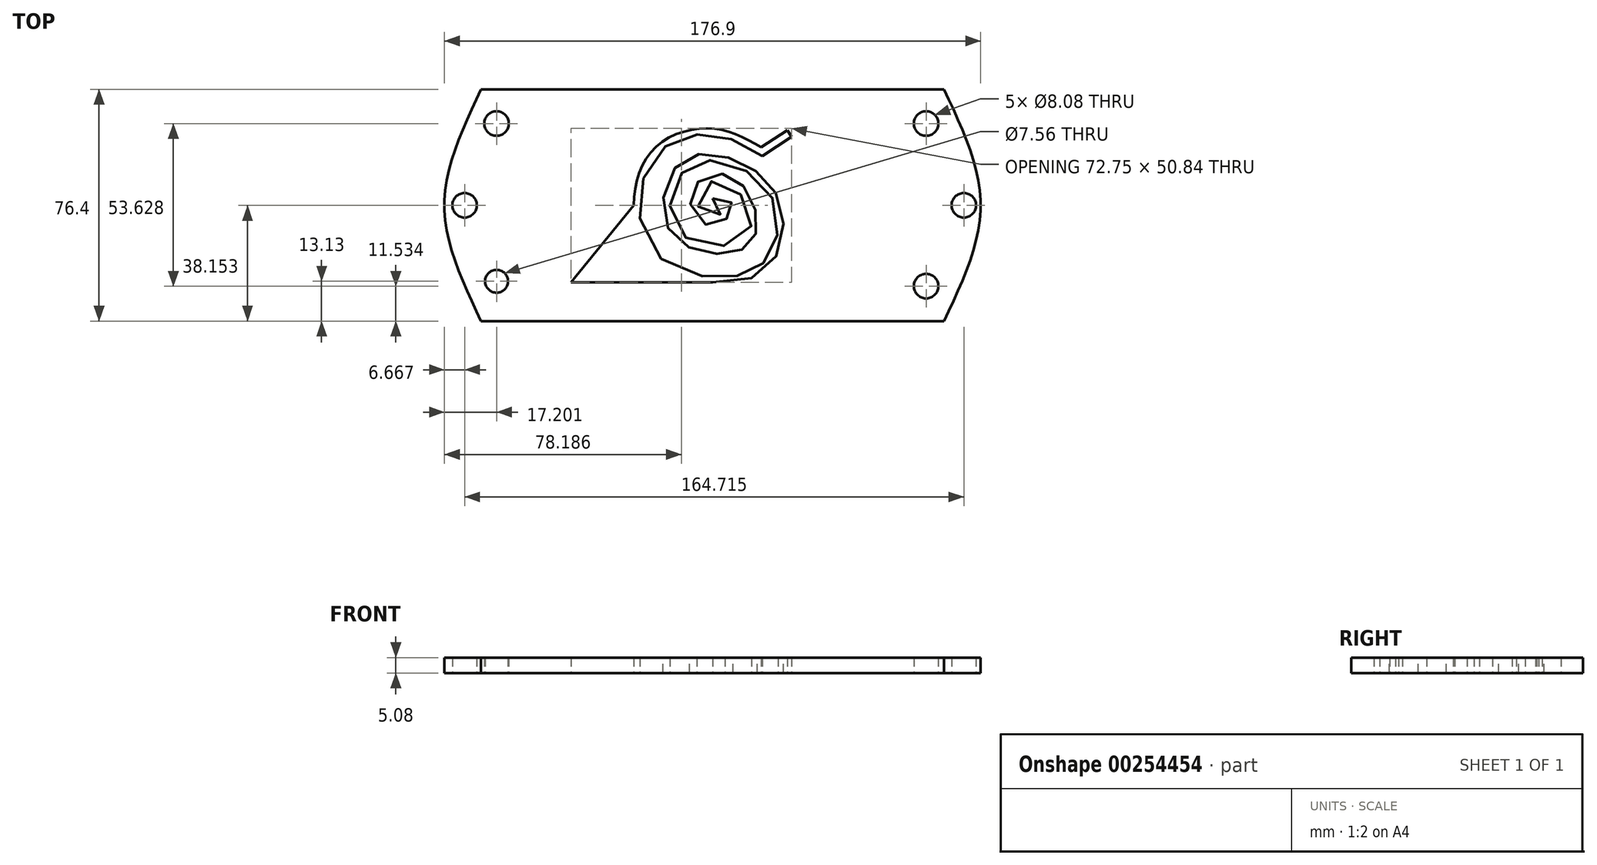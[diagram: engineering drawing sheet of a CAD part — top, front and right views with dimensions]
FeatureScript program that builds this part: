
annotation { "Feature Type Name" : "Feature", "Feature Type Description" : "" }
export const myFeature = defineFeature(function(context is Context, id is Id, definition is map)
    precondition{}
    {
        {
            var Q0;
            Q0=qCreatedBy(makeId("Top.planeOp"),FACE);
            var sketch = newSketch(context, id + "F0", { "sketchPlane" : qUnion([Q0])});
            skLineSegment(sketch, "E0.top", {"start": v(0, 38.2) * mm, "end": v(-76.4, 38.2) * mm});
            skLineSegment(sketch, "E1.MirrorCS", {"start": v(0, -38.2) * mm, "end": v(-76.4, -38.2) * mm});
            skFitSpline(sketch, "E2", {"points": [v(-76.4, 38.2) * mm, v(-88.45, 0) * mm, v(-76.4, -38.2) * mm], "startDerivative": vector(-36.19, -76.4) * mm, "endDerivative": vector(36.19, -76.4) * mm});
            skPoint(sketch, "E3.MirrorCS.start.orphan", {"position": v(-76.4, 0) * mm});
            skPoint(sketch, "E4.MirrorP", {"position": v(76.4, 0) * mm});
            skFitSpline(sketch, "E5.MirrorCS", {"points": [v(76.4, 38.2) * mm, v(88.45, 0) * mm, v(76.4, -38.2) * mm], "startDerivative": vector(36.19, -76.4) * mm, "endDerivative": vector(-36.19, -76.4) * mm});
            skLineSegment(sketch, "E6.MirrorCS", {"start": v(0, 38.2) * mm, "end": v(76.4, 38.2) * mm});
            skLineSegment(sketch, "E7.MirrorCS", {"start": v(0, -38.2) * mm, "end": v(76.4, -38.2) * mm});
            skPoint(sketch, "E8.MirrorCS.end.orphan", {"position": v(0, 38.2) * mm});
            skPoint(sketch, "E8.MirrorCS.start.orphan", {"position": v(0, 0) * mm});
            skLineSegment(sketch, "E9", {"start": v(16.08, 19.16) * mm, "end": v(24.66, 24.8) * mm});
            skFitSpline(sketch, "E10", {"points": [v(16.08, 19.16) * mm, v(0, 25.33) * mm, v(-18.76, 19.16) * mm, v(-26, 0) * mm, v(-17.15, -19.7) * mm, v(16.08, -22.38) * mm, v(22.52, 0) * mm, v(8.3, 14.6) * mm, v(-10.45, 14.34) * mm, v(-15.28, -6.3) * mm, v(0, -15.95) * mm, v(12.87, -12.2) * mm, v(13.67, 0) * mm, v(3.48, 10.32) * mm, v(-7.5, 3.35) * mm, v(0, -6.84) * mm, v(6.7, 0) * mm, v(0, 2.28) * mm], "startDerivative": vector(-255.12, 143) * mm, "endDerivative": vector(-251.77, 14.65) * mm});
            skLineSegment(sketch, "E11", {"start": v(0, -25.47) * mm, "end": v(-46.64, -25.47) * mm});
            skLineSegment(sketch, "E12", {"start": v(-26, 0) * mm, "end": v(-46.64, -25.47) * mm});
            skCircle(sketch, "E13", {"center": v(-71.25, 26.96) * mm, "radius": 4.04 * mm});
            skCircle(sketch, "E14", {"center": v(-81.78, 0) * mm, "radius": 4.04 * mm});
            skCircle(sketch, "E15", {"center": v(-71.25, -25.07) * mm, "radius": 3.78 * mm});
            skCircle(sketch, "E16", {"center": v(70.48, 26.96) * mm, "radius": 4.04 * mm});
            skCircle(sketch, "E17", {"center": v(82.93, 0) * mm, "radius": 4.04 * mm});
            skCircle(sketch, "E18", {"center": v(70.48, -26.67) * mm, "radius": 4.04 * mm});
            skFitSpline(sketch, "E19", {"points": [v(-18.35, 81.74) * mm, v(-34.43, 87.9) * mm, v(-53.2, 81.74) * mm, v(-60.43, 62.57) * mm, v(-51.59, 42.87) * mm, v(-18.35, 40.2) * mm, v(-11.92, 62.57) * mm, v(-26.12, 77.18) * mm, v(-44.89, 76.91) * mm, v(-49.71, 56.27) * mm, v(-34.43, 46.62) * mm, v(-21.57, 50.38) * mm, v(-20.76, 62.57) * mm, v(-30.95, 72.9) * mm, v(-41.94, 65.92) * mm, v(-34.43, 55.74) * mm, v(-27.73, 62.57) * mm, v(-34.43, 64.85) * mm], "startDerivative": vector(-255.12, 143) * mm, "endDerivative": vector(-251.77, 14.65) * mm});
            skLineSegment(sketch, "E20", {"start": v(24.66, 24.8) * mm, "end": v(26.11, 22.58) * mm});
            skLineSegment(sketch, "E21", {"start": v(26.11, 22.58) * mm, "end": v(17.92, 17.2) * mm});
            skLineSegment(sketch, "E22", {"start": v(17.92, 17.2) * mm, "end": v(16.38, 16.2) * mm});
            skFitSpline(sketch, "E23", {"points": [v(16.38, 16.2) * mm, v(9.76, 20.15) * mm, v(2.94, 22.91) * mm, v(-4.42, 23.46) * mm, v(-11.8, 21.62) * mm, v(-17.5, 17.75) * mm, v(-22.66, 9.28) * mm, v(-23.95, 0) * mm, v(-22.3, -10.98) * mm, v(-11.6, -21.1) * mm, v(-1.48, -23.5) * mm, v(5.9, -23.5) * mm, v(12.15, -22.21) * mm, v(16.08, -19.7) * mm, v(19.7, -15.22) * mm, v(21.55, -8.77) * mm, v(20.8, 0) * mm, v(16.38, 7.07) * mm, v(9.02, 12.41) * mm, v(0, 14.8) * mm, v(-4.06, 14.34) * mm, v(-10.45, 10.39) * mm, v(-13.82, 3.39) * mm, v(-13.27, -4.16) * mm, v(-8.66, -10.8) * mm, v(0, -13.19) * mm, v(9.39, -12.08) * mm, v(12.87, -5.82) * mm, v(11.05, 0) * mm, v(6.63, 6.89) * mm, v(0, 8) * mm, v(-4.8, 3.94) * mm, v(-4.24, -1.4) * mm, v(0, -4.53) * mm, v(3.31, -2.14) * mm, v(4.05, 0) * mm, v(0, 2.28) * mm], "startDerivative": vector(-229.5, 144.53) * mm, "endDerivative": vector(-246.5, 94.05) * mm});
            skSolve(sketch);
        }
        {
            var Q0;
            Q0 = qSketchRegion(id + "F0", true);
            extrude(context, id + "F1", {"entities" : qUnion([Q0]), "depth" : 5.08 * mm});
        }
        {
            var Q0;
            Q0 = qSketchRegion(id + "F0", true);
            extrude(context, id + "F2", {"entities" : qUnion([Q0]), "operationType" : NewBodyOperationType.ADD, "depth" : 5.08 * mm});
        }
    });
